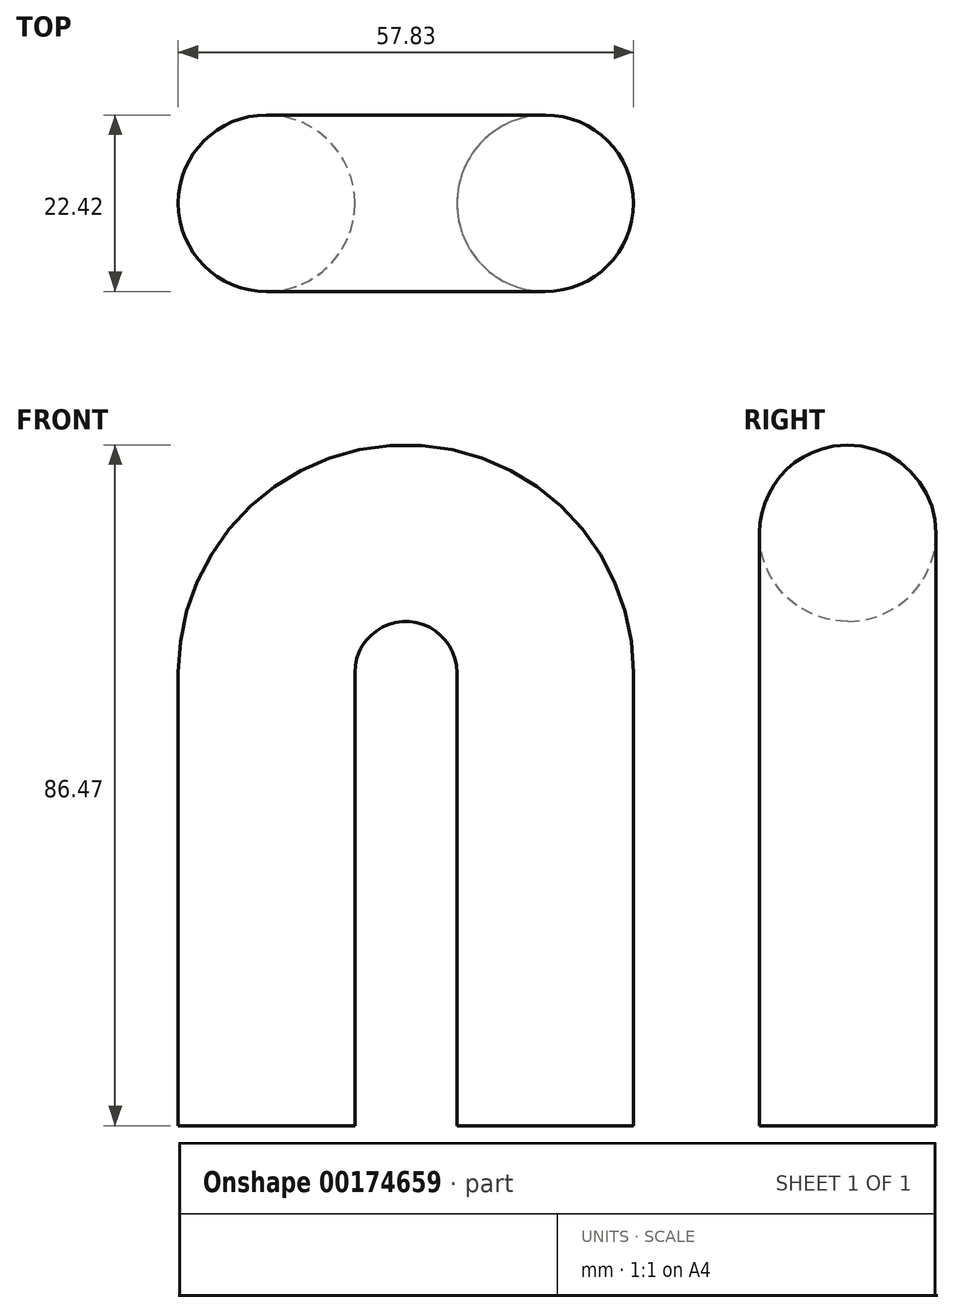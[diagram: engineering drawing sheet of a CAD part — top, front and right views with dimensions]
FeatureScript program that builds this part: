
annotation { "Feature Type Name" : "Feature", "Feature Type Description" : "" }
export const myFeature = defineFeature(function(context is Context, id is Id, definition is map)
    precondition{}
    {
        {
            var Q0;
            Q0=qCreatedBy(makeId("Front.planeOp"),FACE);
            var sketch = newSketch(context, id + "F0", { "sketchPlane" : qUnion([Q0])});
            skLineSegment(sketch, "E0.left", {"start": v(-27.92, -11.51) * mm, "end": v(-27.92, 46.05) * mm});
            skLineSegment(sketch, "E0.right", {"start": v(7.48, -11.51) * mm, "end": v(7.48, 46.05) * mm});
            skArc(sketch, "E1", {"start": v(7.48, 46.05) * mm, "mid": v(-10.22, 63.75) * mm, "end": v(-27.92, 46.05) * mm});
            skSolve(sketch);
        }
        {
            var Q0;
            Q0=qCreatedBy(makeId("Top.planeOp"),FACE);
            var sketch = newSketch(context, id + "F1", { "sketchPlane" : qUnion([Q0])});
            skCircle(sketch, "E2", {"center": v(-27.92, 0) * mm, "radius": 11.21 * mm});
            skSolve(sketch);
        }
        {
            var Q0;
            Q0=makeQuery(id+"F1.imprint","IMPRINT",FACE,{"disambiguationData":[TD([[makeQuery(id+"F1.imprint","IMPRINT",EDGE,{"derivedFrom":sQuery(id+"F1.wireOp",EDGE,"E2")}),1.0]])]});
            var Q1;
            Q1=sQuery(id+"F0.wireOp",EDGE,"E0.left");
            var Q2;
            Q2=sQuery(id+"F0.wireOp",EDGE,"E1");
            var Q3;
            Q3=sQuery(id+"F0.wireOp",EDGE,"E0.right");
            sweep(context, id + "F2", {"profiles" : qUnion([Q0]), "path" : qUnion([Q1, Q2, Q3])});
        }
    });
